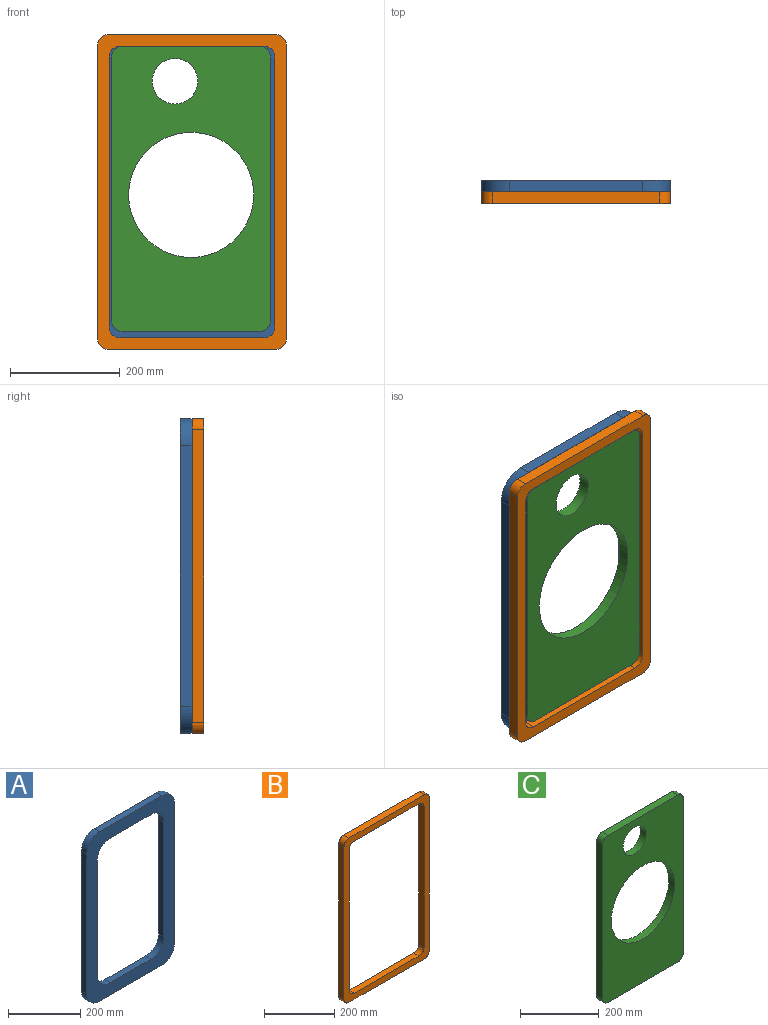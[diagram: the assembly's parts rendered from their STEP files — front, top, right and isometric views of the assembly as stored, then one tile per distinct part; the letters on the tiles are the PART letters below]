
ASSEMBLY  parts=3 mates=2
PART A: 18 faces, bbox 344x21x574 mm
  f0: plane 244x21mm, normal (0,0,1), area 5124mm2, adj f8,f9,f14,f17
  f1: plane 474x21mm, normal (-1,0,0), area 9954mm2, adj f8,f9,f14,f15
  f2: plane 244x21mm, normal (0,0,-1), area 5124mm2, adj f8,f9,f15,f16
  f3: plane 390x21mm, normal (1,0,0), area 8190mm2, adj f8,f9,f10,f13
  f4: plane 160x21mm, normal (0,0,-1), area 3360mm2, adj f8,f9,f10,f11
  f5: plane 390x21mm, normal (-1,0,0), area 8190mm2, adj f8,f9,f11,f12
  f6: plane 160x21mm, normal (0,0,1), area 3360mm2, adj f8,f9,f12,f13
  f7: plane 474x21mm, normal (1,0,0), area 9954mm2, adj f8,f9,f16,f17
  f8: plane 574x344mm, normal (0,-1,0), area 70056mm2, adj f0,f1,f2,f3,f4,f5,f6,f7
  f9: plane 574x344mm, normal (0,1,0), area 70056mm2, adj f0,f1,f2,f3,f4,f5,f6,f7
  f10: cylinder r=50mm len=50mm, axis (0,1,0), area 1649.3mm2, adj f3,f4,f8,f9
  f11: cylinder r=50mm len=50mm, axis (0,-1,0), area 1649.3mm2, adj f4,f5,f8,f9
  f12: cylinder r=50mm len=50mm, axis (0,1,0), area 1649.3mm2, adj f5,f6,f8,f9
  f13: cylinder r=50mm len=50mm, axis (0,-1,0), area 1649.3mm2, adj f3,f6,f8,f9
  f14: cylinder r=50mm len=50mm, axis (0,-1,0), area 1649.3mm2, adj f0,f1,f8,f9
  f15: cylinder r=50mm len=50mm, axis (0,1,0), area 1649.3mm2, adj f1,f2,f8,f9
  f16: cylinder r=50mm len=50mm, axis (0,-1,0), area 1649.3mm2, adj f2,f7,f8,f9
  f17: cylinder r=50mm len=50mm, axis (0,1,0), area 1649.3mm2, adj f0,f7,f8,f9
PART B: 18 faces, bbox 344x21x574 mm
  f0: plane 574x344mm, normal (0,-1,0), area 36792mm2, adj f2,f3,f4,f5,f6,f7,f8,f9
  f1: plane 574x344mm, normal (0,1,0), area 36792mm2, adj f2,f3,f4,f5,f6,f7,f8,f9
  f2: plane 304x21mm, normal (0,0,1), area 6384mm2, adj f0,f1,f14,f17
  f3: plane 534x21mm, normal (-1,0,0), area 11214mm2, adj f0,f1,f14,f15
  f4: plane 304x21mm, normal (0,0,-1), area 6384mm2, adj f0,f1,f15,f16
  f5: plane 534x21mm, normal (1,0,0), area 11214mm2, adj f0,f1,f16,f17
  f6: plane 262x21mm, normal (0,0,-1), area 5502mm2, adj f0,f1,f10,f13
  f7: plane 492x21mm, normal (1,0,0), area 10332mm2, adj f0,f1,f10,f11
  f8: plane 262x21mm, normal (0,0,1), area 5502mm2, adj f0,f1,f11,f12
  f9: plane 492x21mm, normal (-1,0,0), area 10332mm2, adj f0,f1,f12,f13
  f10: cylinder r=20mm len=21mm, axis (0,-1,0), area 659.7mm2, adj f0,f1,f6,f7
  f11: cylinder r=20mm len=21mm, axis (0,1,0), area 659.7mm2, adj f0,f1,f7,f8
  f12: cylinder r=20mm len=21mm, axis (0,-1,0), area 659.7mm2, adj f0,f1,f8,f9
  f13: cylinder r=20mm len=21mm, axis (0,1,0), area 659.7mm2, adj f0,f1,f6,f9
  f14: cylinder r=20mm len=21mm, axis (0,-1,0), area 659.7mm2, adj f0,f1,f2,f3
  f15: cylinder r=20mm len=21mm, axis (0,1,0), area 659.7mm2, adj f0,f1,f3,f4
  f16: cylinder r=20mm len=21mm, axis (0,-1,0), area 659.7mm2, adj f0,f1,f4,f5
  f17: cylinder r=20mm len=21mm, axis (0,1,0), area 659.7mm2, adj f0,f1,f2,f5
PART C: 12 faces, bbox 290x21x520 mm
  f0: plane 250x21mm, normal (0,0,1), area 5250mm2, adj f4,f5,f6,f9
  f1: plane 480x21mm, normal (-1,0,0), area 10080mm2, adj f4,f5,f6,f7
  f2: plane 250x21mm, normal (0,0,-1), area 5250mm2, adj f4,f5,f7,f8
  f3: plane 480x21mm, normal (1,0,0), area 10080mm2, adj f4,f5,f8,f9
  f4: plane 520x290mm, normal (0,-1,0), area 104217.9mm2, adj f0,f1,f2,f3,f6,f7,f8,f9
  f5: plane 520x290mm, normal (0,1,0), area 104217.9mm2, adj f0,f1,f2,f3,f6,f7,f8,f9
  f6: cylinder r=20mm len=21mm, axis (0,-1,0), area 659.7mm2, adj f0,f1,f4,f5
  f7: cylinder r=20mm len=21mm, axis (0,1,0), area 659.7mm2, adj f1,f2,f4,f5
  f8: cylinder r=20mm len=21mm, axis (0,-1,0), area 659.7mm2, adj f2,f3,f4,f5
  f9: cylinder r=20mm len=21mm, axis (0,1,0), area 659.7mm2, adj f0,f3,f4,f5
  f10: cylinder r=114mm len=228mm, axis (0,-1,0), area 15041.9mm2, adj f4,f5
  f11: cylinder r=41.5mm len=83mm, axis (0,-1,0), area 5475.8mm2, adj f4,f5
PLACE A t=(598.74,175.21,51.69)mm
PLACE B t=(598.74,154.21,51.69)mm
PLACE C t=(597.21,154.21,57.52)mm
MATE fastened A.f8 <-> B.f1  axis (0,-1,0) through (598.74,154.21,51.69)mm
MATE fastened A.f8 <-> C.f5  axis (0,-1,0) through (598.74,154.21,51.69)mm
